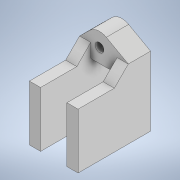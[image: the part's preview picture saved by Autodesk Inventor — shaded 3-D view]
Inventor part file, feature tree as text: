
AUTODESK INVENTOR PART (.ipt)
format: ipt  version: 2022 (Build 260153000, 153)  size: 140,800 bytes
history: native  units: in
note: dims shown in document units (in); Inventor stores cm internally (conversion verified against a paired STEP export)
features: extrude x2, sketch x2, chamfer x1, projected_geometry x1
ambient origin geometry x8: Origin, YZ Plane, XZ Plane, XY Plane, X Axis, Y Axis, Z Axis, Center Point
bodies: Body1 (feature_tree)
feature tree (6):
  extrude  "Extrusion2"  Depth=0.079in
  extrude  "Extrusion3"  Depth=0.65in TaperAngle=0.0deg
  chamfer  "Chamfer1"  Distance=0.2362in
  sketch  "Sketch1"  dims[d0=0.25in d1=0.079in]
  sketch  "Sketch2"  dims[d2=0.0689in d8=0.65in d9=0.0in d10=0.2362in d11=0.1in d12=0.1in d13=0.45in d14=0.0in d15=0.125in d16=0.125in d17=45.0deg]
  projected_geometry  "Projected Loop1"
